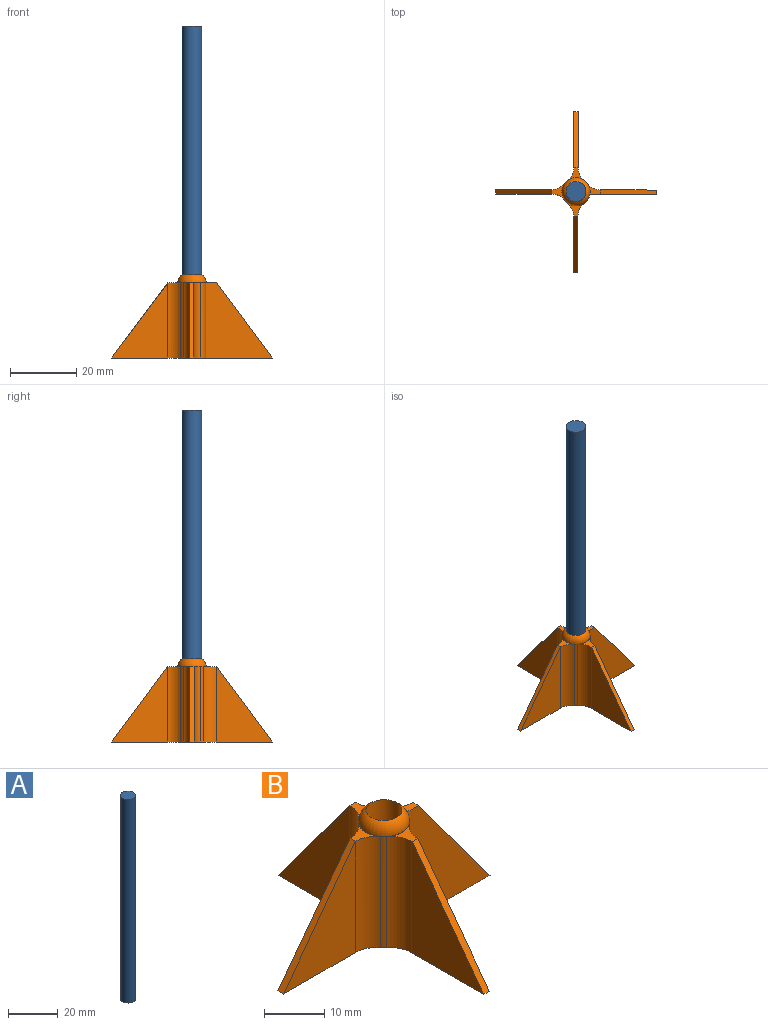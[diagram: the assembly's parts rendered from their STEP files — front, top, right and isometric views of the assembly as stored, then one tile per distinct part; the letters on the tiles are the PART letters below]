
ASSEMBLY  parts=2 mates=1
PART A: 3 faces, bbox 6x6x100 mm
  f0: cylinder r=3mm len=100mm, axis (0,0,-1), area 1885mm2, adj f1,f2
  f1: plane 6x6mm, normal (0,0,1), area 28.3mm2, adj f0
  f2: plane 6x6mm, normal (0,0,-1), area 28.3mm2, adj f0
PART B: 28 faces, bbox 48.4x48.4x25 mm
  f0: plane 22.6x16.9mm, normal (0,1,0), area 191mm2, adj f10,f23,f27
  f1: plane 22.6x16.81mm, normal (1,0,0), area 189.9mm2, adj f10,f19,f26
  f2: plane 22.6x16.92mm, normal (-1,0,0), area 192.5mm2, adj f10,f15,f18,f26
  f3: plane 22.6x16.87mm, normal (1,0,0), area 190.6mm2, adj f10,f21,f25
  f4: plane 22.6x16.85mm, normal (0,1,0), area 190.4mm2, adj f10,f20,f24
  f5: plane 22.6x20mm, normal (0,-1,0), area 261.6mm2, adj f10,f13,f14,f24
  f6: plane 5.19x3.97mm, normal (0,0,1), area 6.7mm2, adj f8,f12,f21,f22,f25
  f7: plane 5.19x3.94mm, normal (0,0,1), area 6.6mm2, adj f8,f17,f23,f27
  f8: cylinder r=4.25mm len=22.62mm, axis (0,0,-1), area 149.2mm2, adj f6,f7,f10,f11,f13,f14,f15,f17
  f9: cylinder r=3mm len=25mm, axis (0,0,-1), area 471.2mm2, adj f10,f11
  f10: plane 48.4x48.39mm, normal (0,0,-1), area 141.6mm2, adj f0,f1,f2,f3,f4,f5,f8,f9
  f11: torus R=1.35mm, axis (0,0,1), area 67.2mm2, adj f8,f9
  f12: plane 22.6x16.88mm, normal (-1,0,0), area 190.9mm2, adj f6,f10,f22,f25
  f13: plane 22.6x0.1mm, normal (-1,0,0), area 2.2mm2, adj f5,f8,f10,f14
  f14: plane 3.98x3.27mm, normal (0,0,1), area 5.4mm2, adj f5,f8,f13,f20,f24
  f15: plane 5.19x4.04mm, normal (0,0,1), area 6.7mm2, adj f2,f8,f18,f19,f26
  f16: plane 22.52x16.84mm, normal (0,-1,0), area 189.6mm2, adj f10,f17,f27
  f17: cylinder r=5mm len=22.6mm, axis (0,0,-1), area 103.8mm2, adj f7,f8,f10,f16,f27
  f18: cylinder r=5mm len=22.6mm, axis (0,0,-1), area 102.1mm2, adj f2,f8,f10,f15
  f19: cylinder r=5mm len=22.6mm, axis (0,0,-1), area 104.4mm2, adj f1,f8,f10,f15
  f20: cylinder r=5mm len=22.6mm, axis (0,0,-1), area 104mm2, adj f4,f8,f10,f14
  f21: cylinder r=5mm len=22.6mm, axis (0,0,-1), area 103.4mm2, adj f3,f6,f8,f10
  f22: cylinder r=5mm len=22.6mm, axis (0,0,-1), area 103.1mm2, adj f6,f8,f10,f12
  f23: cylinder r=5mm len=22.6mm, axis (0,0,-1), area 102.7mm2, adj f0,f7,f8,f10
  f24: plane 22.6x16.85mm, normal (0.8,0,0.6), area 36.6mm2, adj f4,f5,f10,f14
  f25: plane 22.6x16.87mm, normal (0,0.8,0.6), area 36.7mm2, adj f3,f6,f10,f12
  f26: plane 22.6x16.81mm, normal (0,-0.8,0.6), area 36.6mm2, adj f1,f2,f10,f15
  f27: plane 22.6x16.9mm, normal (-0.8,0,0.6), area 36.7mm2, adj f0,f7,f10,f16,f17
PLACE A t=(-19.25,-8.3,0.13)mm fixed
PLACE B t=(-19.25,-8.3,0.13)mm
MATE fastened A.f0 <-> B.f9  axis (0,0,-1) through (-19.25,-8.3,0.13)mm
